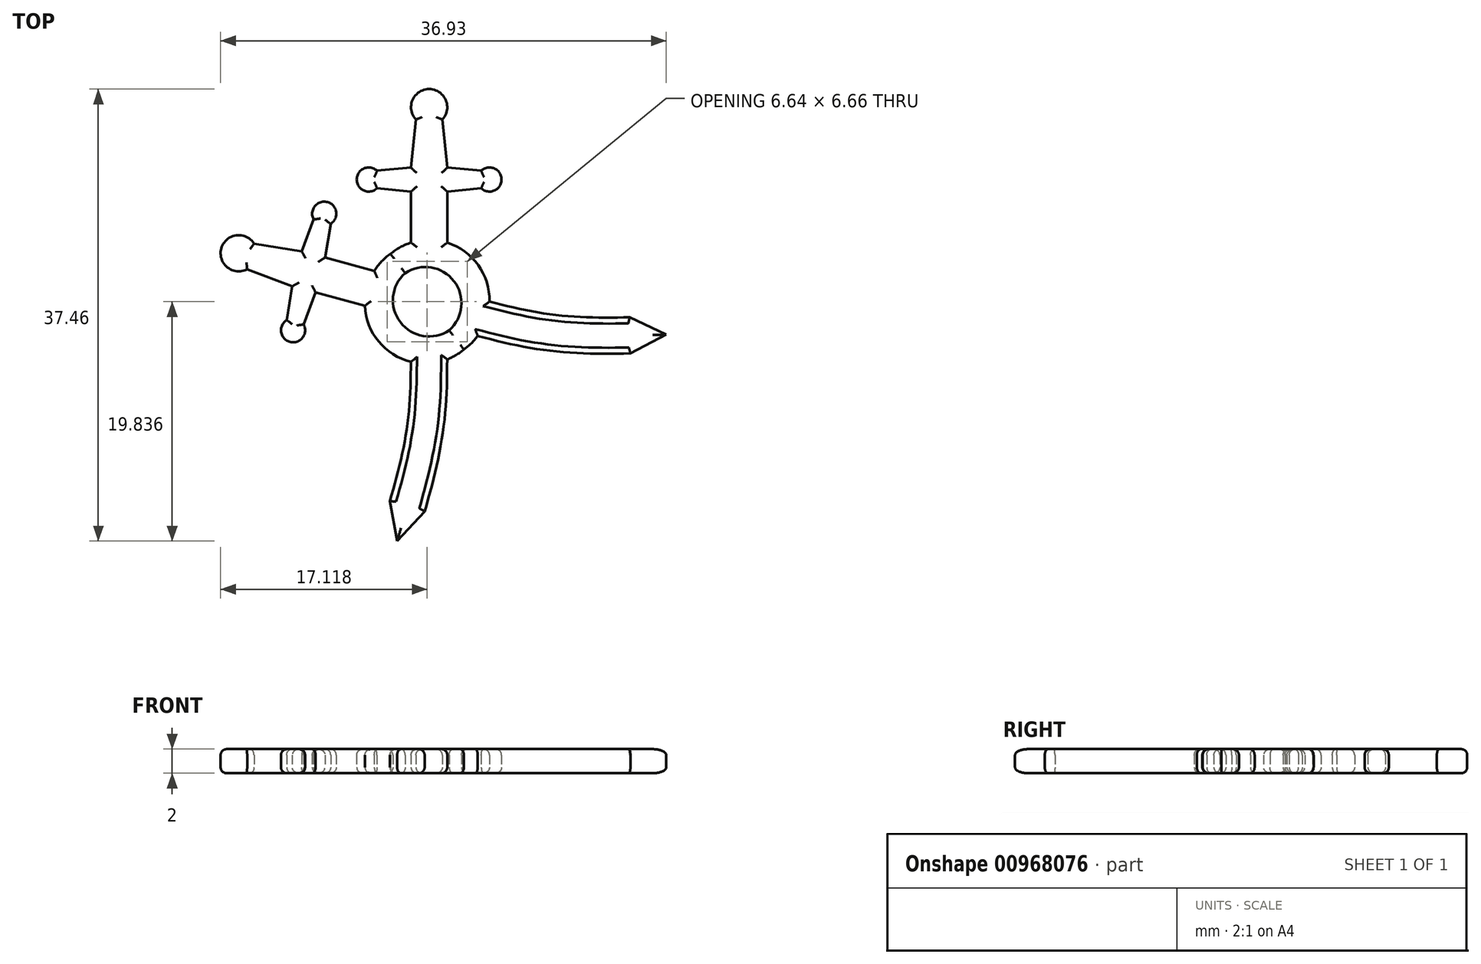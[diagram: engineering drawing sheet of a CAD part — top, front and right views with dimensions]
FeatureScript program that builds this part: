
annotation { "Feature Type Name" : "Feature", "Feature Type Description" : "" }
export const myFeature = defineFeature(function(context is Context, id is Id, definition is map)
    precondition{}
    {
        {
            assignVariable(context, id + "F0", {"name" : "thickness", "anyValue" : 2});
        }
        {
            var Q0;
            Q0=qCreatedBy(makeId("Top.planeOp"),FACE);
            var sketch = newSketch(context, id + "F1", { "sketchPlane" : qUnion([Q0])});
            skCircle(sketch, "E0", {"center": v(0, 0) * mm, "radius": 5 * mm});
            skCircle(sketch, "E1", {"center": v(0, 0) * mm, "radius": 3 * mm});
            skLineSegment(sketch, "E2.left", {"start": v(0, 16) * mm, "end": v(0, 5) * mm});
            skLineSegment(sketch, "E3", {"start": v(0, 10) * mm, "end": v(-5, 10) * mm, "construction": true});
            skLineSegment(sketch, "E4", {"start": v(-5, 10) * mm, "end": v(-5, 10.67) * mm});
            skLineSegment(sketch, "E5.MirrorCS", {"start": v(-5, 10) * mm, "end": v(-5, 9.33) * mm});
            skLineSegment(sketch, "E6", {"start": v(-1.5, 10) * mm, "end": v(-1.5, 11) * mm, "construction": true});
            skLineSegment(sketch, "E7", {"start": v(-5, 10.67) * mm, "end": v(-1.5, 11) * mm});
            skLineSegment(sketch, "E8.MirrorCS", {"start": v(-5, 9.33) * mm, "end": v(-1.5, 9) * mm});
            skCircle(sketch, "E9", {"center": v(-5, 10) * mm, "radius": 1 * mm});
            skLineSegment(sketch, "E10.bottom", {"start": v(0, 10) * mm, "end": v(-1.5, 10) * mm});
            skLineSegment(sketch, "E10.left", {"start": v(0, 10) * mm, "end": v(0, 5) * mm});
            skLineSegment(sketch, "E10.right", {"start": v(-1.5, 10) * mm, "end": v(-1.5, 4.77) * mm});
            skLineSegment(sketch, "E11.bottom", {"start": v(0, 16) * mm, "end": v(-1, 16) * mm});
            skLineSegment(sketch, "E11.top", {"start": v(0, 10) * mm, "end": v(-0.75, 10) * mm});
            skLineSegment(sketch, "E11.left", {"start": v(0, 16) * mm, "end": v(0, 10) * mm});
            skLineSegment(sketch, "E12", {"start": v(-1.5, 11) * mm, "end": v(-1, 16) * mm});
            skCircle(sketch, "E13", {"center": v(0, 16) * mm, "radius": 1.5 * mm});
            skLineSegment(sketch, "E14.MirrorCS", {"start": v(1.5, 10) * mm, "end": v(1.5, 4.77) * mm});
            skLineSegment(sketch, "E15.MirrorCS", {"start": v(5, 9.33) * mm, "end": v(1.5, 9) * mm});
            skLineSegment(sketch, "E16.MirrorCS", {"start": v(5, 10.67) * mm, "end": v(1.5, 11) * mm});
            skLineSegment(sketch, "E17.MirrorCS", {"start": v(1.5, 11) * mm, "end": v(1, 16) * mm});
            skCircle(sketch, "E18.MirrorC", {"center": v(5, 10) * mm, "radius": 1 * mm});
            skFitSpline(sketch, "E19", {"points": [v(0, 0) * mm, v(0, -5) * mm, v(-1.82, -17.08) * mm], "startDerivative": vector(0.92, -11.54) * mm, "endDerivative": vector(-8.93, -30.9) * mm});
            skFitSpline(sketch, "E20.0", {"points": [v(1.5, 0.12) * mm, v(1.54, -0.4) * mm, v(1.57, -1.48) * mm, v(1.55, -2.86) * mm, v(1.52, -3.98) * mm, v(1.5, -4.82) * mm, v(1.49, -5.68) * mm, v(1.47, -6.88) * mm, v(1.4, -8.55) * mm, v(1.14, -10.94) * mm, v(0.6, -13.83) * mm, v(0, -16.18) * mm, v(-0.38, -17.5) * mm]});
            skFitSpline(sketch, "E21.0", {"points": [v(-1.5, -0.12) * mm, v(-1.46, -0.55) * mm, v(-1.43, -1.5) * mm, v(-1.45, -2.8) * mm, v(-1.47, -3.9) * mm, v(-1.5, -4.61) * mm, v(-1.5, -5.2) * mm, v(-1.51, -5.78) * mm, v(-1.53, -6.5) * mm, v(-1.56, -7.41) * mm, v(-1.64, -8.7) * mm, v(-1.83, -10.5) * mm, v(-2.32, -13.17) * mm, v(-2.9, -15.4) * mm, v(-3.26, -16.67) * mm]});
            skLineSegment(sketch, "E22", {"start": v(-1.82, -17.08) * mm, "end": v(-2.65, -19.96) * mm, "construction": true});
            skLineSegment(sketch, "E23", {"start": v(-3.26, -16.66) * mm, "end": v(-2.65, -19.96) * mm});
            skLineSegment(sketch, "E24", {"start": v(-0.38, -17.5) * mm, "end": v(-2.65, -19.96) * mm});
            skSolve(sketch);
        }
        {
            var Q0;
            Q0=qCreatedBy(makeId("Top.planeOp"),FACE);
            var sketch = newSketch(context, id + "F2", { "sketchPlane" : qUnion([Q0])});
            skLineSegment(sketch, "E25", {"start": v(-9.83, 12.48) * mm, "end": v(13.59, -18.04) * mm, "construction": true});
            skSolve(sketch);
        }
        {
            var Q0;
            Q0=sQuery(id+"F2.wireOp",EDGE,"E25");
            var Q1;
            Q1=qCreatedBy(makeId("Top.planeOp"),FACE);
            cPlane(context, id + "F3", {"entities" : qUnion([Q0, Q1]), "cplaneType" : CPlaneType.LINE_ANGLE, "offset" : 25 * mm, "angle" : 90 * degree, "width" : 150 * mm, "height" : 150 * mm});
        }
        {
            var Q0;
            Q0 = qSketchRegion(id + "F1", true);
            extrude(context, id + "F4", {"entities" : qUnion([Q0]), "depth" : (getVariable(context, 'thickness')) * mm, "offsetDistance" : 25 * mm});
        }
        {
            var Q0;
            Q0=makeQuery(id+"F4.opExtrude","SWEPT_BODY",BODY,{"disambiguationData":[OSD([sQuery(id+"F1.wireOp",EDGE,"E0"),sQuery(id+"F1.wireOp",EDGE,"E1"),sQuery(id+"F1.wireOp",EDGE,"E7"),sQuery(id+"F1.wireOp",EDGE,"E8.MirrorCS"),sQuery(id+"F1.wireOp",EDGE,"E9"),sQuery(id+"F1.wireOp",EDGE,"E10.right"),sQuery(id+"F1.wireOp",EDGE,"E12"),sQuery(id+"F1.wireOp",EDGE,"E13"),sQuery(id+"F1.wireOp",EDGE,"E14.MirrorCS"),sQuery(id+"F1.wireOp",EDGE,"E15.MirrorCS"),sQuery(id+"F1.wireOp",EDGE,"E16.MirrorCS"),sQuery(id+"F1.wireOp",EDGE,"E17.MirrorCS"),sQuery(id+"F1.wireOp",EDGE,"E18.MirrorC"),sQuery(id+"F1.wireOp",EDGE,"E20.0"),sQuery(id+"F1.wireOp",EDGE,"E21.0"),sQuery(id+"F1.wireOp",EDGE,"E23"),sQuery(id+"F1.wireOp",EDGE,"E24")])]});
            var Q1;
            Q1=qCreatedBy(id+"F3.planeOp",FACE);
            mirror(context, id + "F5", {"operationType" : NewBodyOperationType.ADD, "entities" : qUnion([Q0]), "mirrorPlane" : qUnion([Q1])});
        }
        {
            var Q0;
            {var subQ0=makeQuery(id+"F4.opExtrude","CAP_FACE",FACE,{"disambiguationData":[OSD([sQuery(id+"F1.wireOp",EDGE,"E0"),sQuery(id+"F1.wireOp",EDGE,"E1"),sQuery(id+"F1.wireOp",EDGE,"E7"),sQuery(id+"F1.wireOp",EDGE,"E8.MirrorCS"),sQuery(id+"F1.wireOp",EDGE,"E9"),sQuery(id+"F1.wireOp",EDGE,"E10.right"),sQuery(id+"F1.wireOp",EDGE,"E12"),sQuery(id+"F1.wireOp",EDGE,"E13"),sQuery(id+"F1.wireOp",EDGE,"E14.MirrorCS"),sQuery(id+"F1.wireOp",EDGE,"E15.MirrorCS"),sQuery(id+"F1.wireOp",EDGE,"E16.MirrorCS"),sQuery(id+"F1.wireOp",EDGE,"E17.MirrorCS"),sQuery(id+"F1.wireOp",EDGE,"E18.MirrorC"),sQuery(id+"F1.wireOp",EDGE,"E20.0"),sQuery(id+"F1.wireOp",EDGE,"E21.0"),sQuery(id+"F1.wireOp",EDGE,"E23"),sQuery(id+"F1.wireOp",EDGE,"E24")])],"isStart":true});Q0=makeQuery(id+"F5.boolean.opBoolean","MERGE",FACE,{"derivedFrom":[subQ0,makeQuery(id+"F5.opPattern","COPY",FACE,{"derivedFrom":subQ0,"instanceName":"1"})]});}
            var Q1;
            {var subQ0=makeQuery(id+"F4.opExtrude","CAP_FACE",FACE,{"disambiguationData":[OSD([sQuery(id+"F1.wireOp",EDGE,"E0"),sQuery(id+"F1.wireOp",EDGE,"E1"),sQuery(id+"F1.wireOp",EDGE,"E7"),sQuery(id+"F1.wireOp",EDGE,"E8.MirrorCS"),sQuery(id+"F1.wireOp",EDGE,"E9"),sQuery(id+"F1.wireOp",EDGE,"E10.right"),sQuery(id+"F1.wireOp",EDGE,"E12"),sQuery(id+"F1.wireOp",EDGE,"E13"),sQuery(id+"F1.wireOp",EDGE,"E14.MirrorCS"),sQuery(id+"F1.wireOp",EDGE,"E15.MirrorCS"),sQuery(id+"F1.wireOp",EDGE,"E16.MirrorCS"),sQuery(id+"F1.wireOp",EDGE,"E17.MirrorCS"),sQuery(id+"F1.wireOp",EDGE,"E18.MirrorC"),sQuery(id+"F1.wireOp",EDGE,"E20.0"),sQuery(id+"F1.wireOp",EDGE,"E21.0"),sQuery(id+"F1.wireOp",EDGE,"E23"),sQuery(id+"F1.wireOp",EDGE,"E24")])],"isStart":false});Q1=makeQuery(id+"F5.boolean.opBoolean","MERGE",FACE,{"derivedFrom":[subQ0,makeQuery(id+"F5.opPattern","COPY",FACE,{"derivedFrom":subQ0,"instanceName":"1"})]});}
            fillet(context, id + "F6", {"entities" : qUnion([Q0, Q1]), "radius" : (getVariable(context, 'thickness') / 4) * mm, "tangentPropagation" : true, "allowEdgeOverflow" : false});
        }
    });
